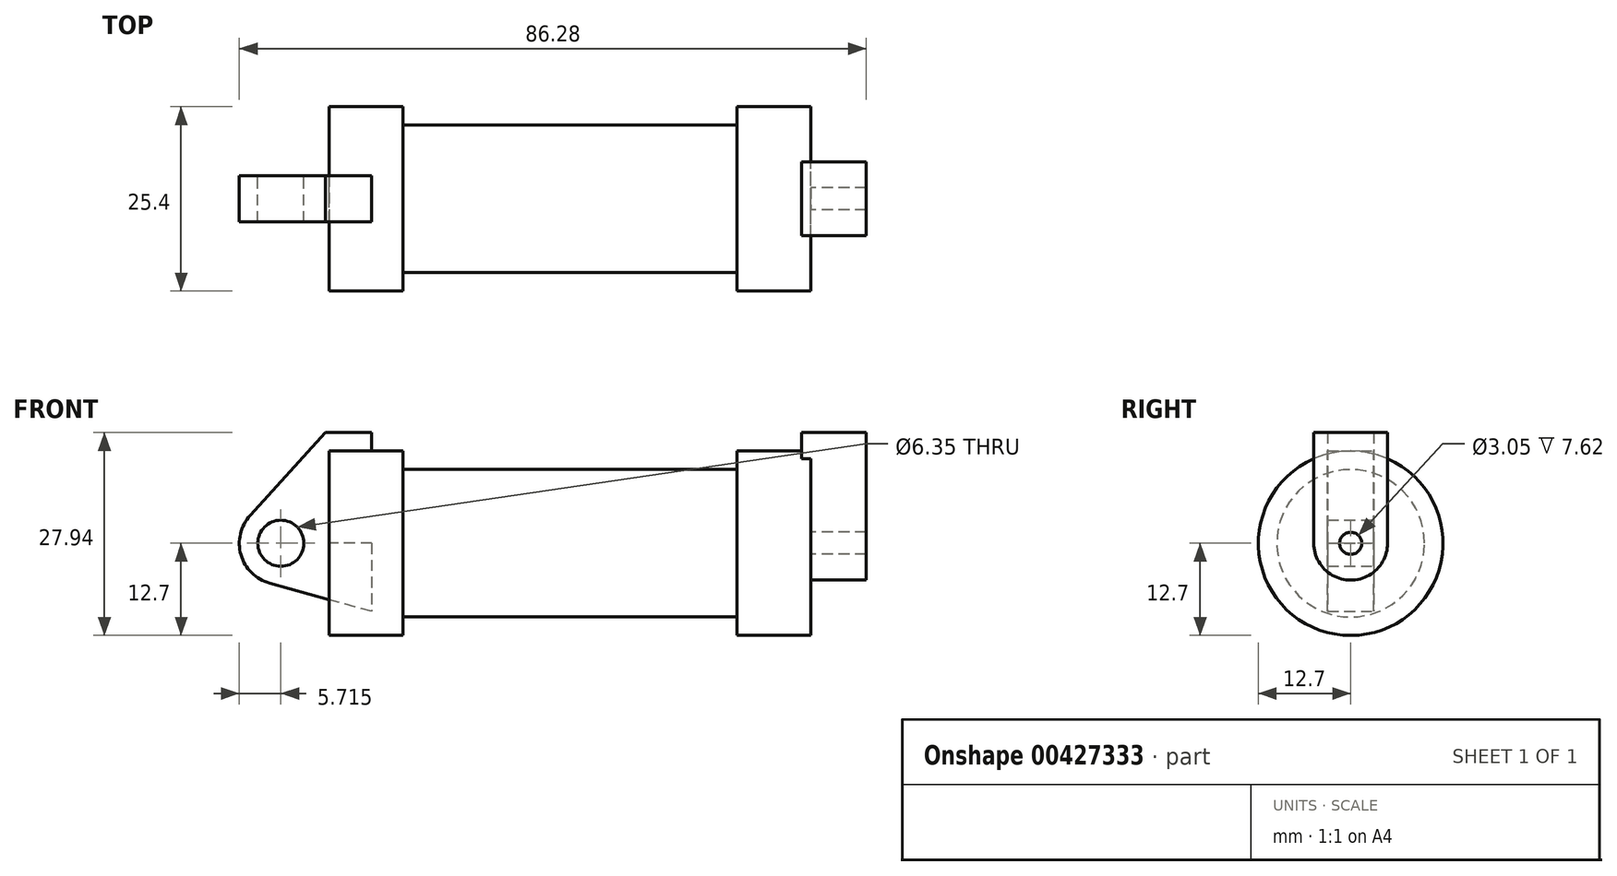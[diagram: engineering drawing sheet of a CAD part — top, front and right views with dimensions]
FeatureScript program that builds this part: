
annotation { "Feature Type Name" : "Feature", "Feature Type Description" : "" }
export const myFeature = defineFeature(function(context is Context, id is Id, definition is map)
    precondition{}
    {
        {
            var Q0;
            Q0=qCreatedBy(makeId("Front.planeOp"),FACE);
            var sketch = newSketch(context, id + "F0", { "sketchPlane" : qUnion([Q0])});
            skLineSegment(sketch, "E0", {"start": v(0, 0) * mm, "end": v(0, 12.7) * mm});
            skLineSegment(sketch, "E1", {"start": v(0, 12.7) * mm, "end": v(10.16, 12.7) * mm});
            skLineSegment(sketch, "E2", {"start": v(10.16, 12.7) * mm, "end": v(10.16, 10.16) * mm});
            skLineSegment(sketch, "E3", {"start": v(10.16, 10.16) * mm, "end": v(56.13, 10.16) * mm});
            skLineSegment(sketch, "E4", {"start": v(56.13, 10.16) * mm, "end": v(56.13, 12.7) * mm});
            skLineSegment(sketch, "E5", {"start": v(56.13, 12.7) * mm, "end": v(66.3, 12.7) * mm});
            skLineSegment(sketch, "E6", {"start": v(66.3, 12.7) * mm, "end": v(66.3, 0) * mm});
            skLineSegment(sketch, "E7", {"start": v(66.3, 0) * mm, "end": v(0, 0) * mm});
            skLineSegment(sketch, "E8", {"start": v(5.84, 15.24) * mm, "end": v(-0.5, 15.24) * mm});
            skLineSegment(sketch, "E9", {"start": v(-0.5, 15.24) * mm, "end": v(-10.88, 3.85) * mm});
            skLineSegment(sketch, "E10", {"start": v(0, 0) * mm, "end": v(-6.65, 0) * mm});
            skCircle(sketch, "E11", {"center": v(-6.65, 0) * mm, "radius": 5.72 * mm});
            skCircle(sketch, "E12", {"center": v(-6.65, 0) * mm, "radius": 3.18 * mm});
            skLineSegment(sketch, "E13", {"start": v(5.84, 15.24) * mm, "end": v(5.84, -9.4) * mm});
            skLineSegment(sketch, "E14", {"start": v(5.84, -9.4) * mm, "end": v(-8.18, -5.5) * mm});
            skSolve(sketch);
        }
        {
            var Q0;
            {var subQ0=sQuery(id+"F0.wireOp",EDGE,"E2");Q0=makeQuery(id+"F0.imprint","IMPRINT",FACE,{"disambiguationData":[TD([[makeQuery(id+"F0.imprint","IMPRINT",EDGE,{"derivedFrom":subQ0}),-1.0]])]});}
            var Q1;
            {var subQ0=sQuery(id+"F0.wireOp",EDGE,"E0");Q1=makeQuery(id+"F0.imprint","IMPRINT",FACE,{"disambiguationData":[TD([[makeQuery(id+"F0.imprint","IMPRINT",EDGE,{"derivedFrom":subQ0}),-1.0]])]});}
            var Q2;
            Q2=sQuery(id+"F0.wireOp",EDGE,"E7");
            revolve(context, id + "F1", {"entities" : qUnion([Q0, Q1]), "axis" : qUnion([Q2]), "revolveType" : RevolveType.FULL});
        }
        {
            var Q0;
            {var subQ5=sQuery(id+"F0.wireOp",EDGE,"E12");Q0=makeQuery(id+"F0.imprint","IMPRINT",FACE,{"disambiguationData":[TD([[makeQuery(id+"F0.imprint","IMPRINT",EDGE,{"derivedFrom":subQ5}),-1.0]])]});}
            var Q1;
            {var subQ1=sQuery(id+"F0.wireOp",EDGE,"E0");Q1=makeQuery(id+"F0.imprint","IMPRINT",FACE,{"disambiguationData":[TD([[makeQuery(id+"F0.imprint","IMPRINT",EDGE,{"derivedFrom":subQ1}),1.0]])]});}
            var Q2;
            {var subQ0=sQuery(id+"F0.wireOp",EDGE,"E14");Q2=makeQuery(id+"F0.imprint","IMPRINT",FACE,{"disambiguationData":[TD([[makeQuery(id+"F0.imprint","IMPRINT",EDGE,{"derivedFrom":subQ0}),-1.0]])]});}
            extrude(context, id + "F2", {"entities" : qUnion([Q0, Q1, Q2]), "endBound" : BoundingType.SYMMETRIC, "depth" : 6.35 * mm});
        }
        {
            var Q0;
            Q0=makeQuery(id+"F1.opRevolve","SWEPT_FACE",FACE,{"disambiguationData":[OSD([sQuery(id+"F0.wireOp",EDGE,"E6")])]});
            var sketch = newSketch(context, id + "F3", { "sketchPlane" : qUnion([Q0])});
            skCircle(sketch, "E15", {"center": v(0, 0) * mm, "radius": 1.52 * mm});
            skCircle(sketch, "E16", {"center": v(0, 0) * mm, "radius": 5.08 * mm});
            skLineSegment(sketch, "E17", {"start": v(-5.08, 0) * mm, "end": v(-5.08, 15.24) * mm});
            skLineSegment(sketch, "E18", {"start": v(-5.08, 15.24) * mm, "end": v(5.08, 15.24) * mm});
            skLineSegment(sketch, "E19", {"start": v(5.08, 15.24) * mm, "end": v(5.08, 0) * mm});
            skSolve(sketch);
        }
        {
            var Q0;
            {var subQ0=sQuery(id+"F3.wireOp",EDGE,"E18");Q0=makeQuery(id+"F3.imprint","IMPRINT",FACE,{"disambiguationData":[TD([[makeQuery(id+"F3.imprint","IMPRINT",EDGE,{"derivedFrom":subQ0}),-1.0]])]});}
            extrude(context, id + "F4", {"entities" : qUnion([Q0]), "operationType" : NewBodyOperationType.ADD, "oppositeDirection" : true, "depth" : 1.27 * mm});
        }
        {
            var Q0;
            Q0 = qSketchRegion(id + "F3", true);
            extrude(context, id + "F5", {"entities" : qUnion([Q0]), "operationType" : NewBodyOperationType.ADD, "depth" : 7.62 * mm});
        }
    });
